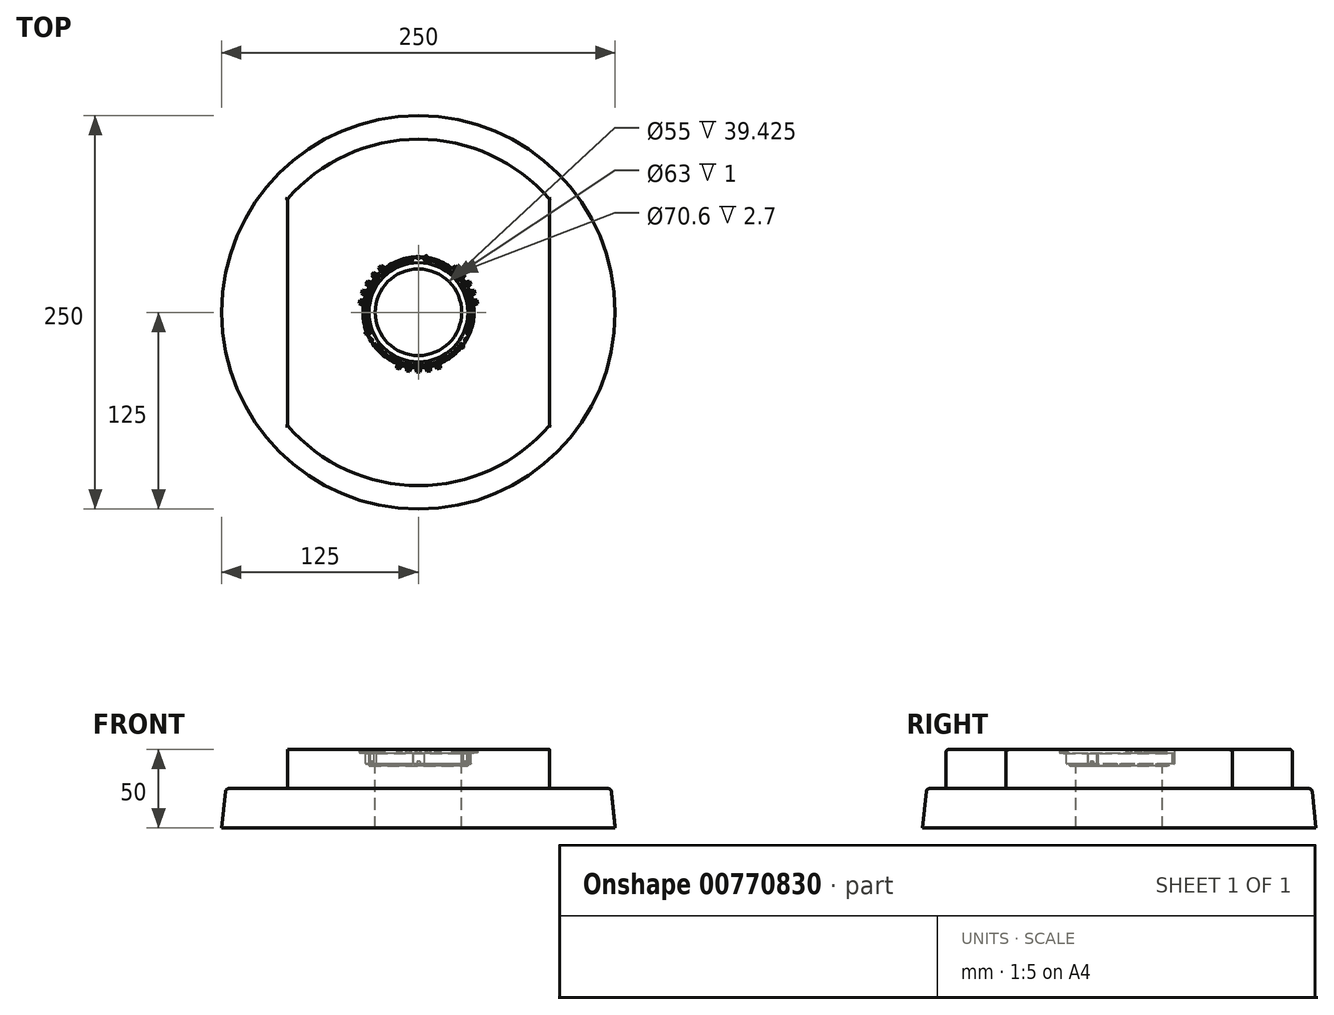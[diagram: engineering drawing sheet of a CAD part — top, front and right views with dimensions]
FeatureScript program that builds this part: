
annotation { "Feature Type Name" : "Feature", "Feature Type Description" : "" }
export const myFeature = defineFeature(function(context is Context, id is Id, definition is map)
    precondition{}
    {
        {
            var Q0;
            Q0=qCreatedBy(makeId("Front.planeOp"),FACE);
            var sketch = newSketch(context, id + "F0", { "sketchPlane" : qUnion([Q0])});
            skLineSegment(sketch, "E0", {"start": v(0, 117.97) * mm, "end": v(0, 0) * mm, "construction": true});
            skLineSegment(sketch, "E1", {"start": v(0, 0) * mm, "end": v(-164.87, 0) * mm, "construction": true});
            skLineSegment(sketch, "E2.bottom", {"start": v(-125, 0) * mm, "end": v(-27.5, 0) * mm});
            skLineSegment(sketch, "E2.top", {"start": v(-110, 50) * mm, "end": v(-37.95, 50) * mm});
            skLineSegment(sketch, "E2.right", {"start": v(0, 0) * mm, "end": v(0, 50) * mm});
            skLineSegment(sketch, "E3", {"start": v(-125, 25) * mm, "end": v(-110, 25) * mm});
            skLineSegment(sketch, "E4", {"start": v(-110, 25) * mm, "end": v(-110, 50) * mm});
            skLineSegment(sketch, "E5", {"start": v(-27.5, 39.43) * mm, "end": v(-27.5, 0) * mm});
            skLineSegment(sketch, "E6", {"start": v(-33.5, 46.85) * mm, "end": v(-33.5, 40.73) * mm});
            skLineSegment(sketch, "E7", {"start": v(-33.5, 40.73) * mm, "end": v(-31.5, 40.73) * mm});
            skLineSegment(sketch, "E8", {"start": v(-31.5, 40.73) * mm, "end": v(-31.5, 39.43) * mm});
            skLineSegment(sketch, "E9", {"start": v(-31.5, 39.43) * mm, "end": v(-27.5, 39.43) * mm});
            skPoint(sketch, "E10.orphan", {"position": v(-27.5, 50) * mm});
            skLineSegment(sketch, "E11", {"start": v(-33.5, 46.85) * mm, "end": v(-33.5, 50) * mm});
            skLineSegment(sketch, "E12", {"start": v(-33.5, 50) * mm, "end": v(-37.95, 50) * mm});
            skLineSegment(sketch, "E13", {"start": v(-125, 0) * mm, "end": v(-125, 25) * mm});
            skLineSegment(sketch, "E14", {"start": v(-125, 0) * mm, "end": v(-122.32, 25) * mm});
            skSolve(sketch);
        }
        {
            var Q0;
            Q0=makeQuery(id+"F0.imprint","IMPRINT",FACE,{"disambiguationData":[TD([[makeQuery(id+"F0.imprint","IMPRINT",EDGE,{"derivedFrom":sQuery(id+"F0.wireOp",EDGE,"E2.bottom")}),1.0]])]});
            var Q1;
            Q1=sQuery(id+"F0.wireOp",EDGE,"E0");
            revolve(context, id + "F1", {"surfaceOperationType" : NewSurfaceOperationType.NEW, "entities" : qUnion([Q0]), "axis" : qUnion([Q1]), "revolveType" : RevolveType.FULL});
        }
        {
            var Q0;
            Q0=makeQuery(id+"F1.opRevolve","SWEPT_FACE",FACE,{"disambiguationData":[OSD([sQuery(id+"F0.wireOp",EDGE,"E2.top"),sQuery(id+"F0.wireOp",EDGE,"E12")])]});
            var sketch = newSketch(context, id + "F2", { "sketchPlane" : qUnion([Q0])});
            skLineSegment(sketch, "E15.bottom", {"start": v(-83.23, 71.92) * mm, "end": v(83.23, 71.92) * mm});
            skLineSegment(sketch, "E15.top", {"start": v(-83.23, -71.92) * mm, "end": v(83.23, -71.92) * mm});
            skLineSegment(sketch, "E15.left", {"start": v(-83.23, 71.92) * mm, "end": v(-83.23, -71.92) * mm});
            skLineSegment(sketch, "E15.right", {"start": v(83.23, 71.92) * mm, "end": v(83.23, -71.92) * mm});
            skPoint(sketch, "E15.middle", {"position": v(0, 0) * mm});
            skCircle(sketch, "E16", {"center": v(0, 0) * mm, "radius": 110 * mm});
            skSolve(sketch);
        }
        {
            var Q0;
            {var subQ0=sQuery(id+"F2.wireOp",EDGE,"E15.right");Q0=makeQuery(id+"F2.imprint","IMPRINT",FACE,{"disambiguationData":[TD([[makeQuery(id+"F2.imprint","IMPRINT",EDGE,{"derivedFrom":subQ0}),1.0]])]});}
            var Q1;
            {var subQ0=sQuery(id+"F2.wireOp",EDGE,"E15.left");Q1=makeQuery(id+"F2.imprint","IMPRINT",FACE,{"disambiguationData":[TD([[makeQuery(id+"F2.imprint","IMPRINT",EDGE,{"derivedFrom":subQ0}),-1.0]])]});}
            extrude(context, id + "F3", {"entities" : qUnion([Q0, Q1]), "operationType" : NewBodyOperationType.REMOVE, "oppositeDirection" : true, "depth" : 25 * mm, "offsetDistance" : 25 * mm});
        }
        {
            var Q0;
            Q0=makeQuery(id+"F3.boolean.opBoolean","SPLIT",EDGE,{"disambiguationData":[OD(1.0)],"derivedFrom":makeQuery(id+"F1.opRevolve","SWEPT_EDGE",EDGE,{"disambiguationData":[OSD([sQuery(id+"F0.wireOp",EDGE,"E2.top"),sQuery(id+"F0.wireOp",EDGE,"E4")])]})});
            var Q1;
            Q1=makeQuery(id+"F3.boolean.opBoolean","COPY",EDGE,{"derivedFrom":makeQuery(id+"F3.opExtrude","CAP_EDGE",EDGE,{"disambiguationData":[OSD([sQuery(id+"F2.wireOp",EDGE,"E15.left")])],"isStart":true})});
            var Q2;
            Q2=makeQuery(id+"F3.boolean.opBoolean","SPLIT",EDGE,{"disambiguationData":[OD(0.0)],"derivedFrom":makeQuery(id+"F1.opRevolve","SWEPT_EDGE",EDGE,{"disambiguationData":[OSD([sQuery(id+"F0.wireOp",EDGE,"E2.top"),sQuery(id+"F0.wireOp",EDGE,"E4")])]})});
            var Q3;
            Q3=makeQuery(id+"F3.boolean.opBoolean","COPY",EDGE,{"derivedFrom":makeQuery(id+"F3.opExtrude","CAP_EDGE",EDGE,{"disambiguationData":[OSD([sQuery(id+"F2.wireOp",EDGE,"E15.right")])],"isStart":true})});
            var Q4;
            Q4=makeQuery(id+"F1.opRevolve","SWEPT_EDGE",EDGE,{"disambiguationData":[OSD([sQuery(id+"F0.wireOp",EDGE,"E3"),sQuery(id+"F0.wireOp",EDGE,"E14")])]});
            fillet(context, id + "F4", {"entities" : qUnion([Q0, Q1, Q2, Q3, Q4]), "radius" : 2 * mm, "tangentPropagation" : true, "allowEdgeOverflow" : false});
        }
        {
            var Q0;
            Q0=makeQuery(id+"F3.boolean.opBoolean","COPY",EDGE,{"derivedFrom":makeQuery(id+"F3.opExtrude","CAP_EDGE",EDGE,{"disambiguationData":[OSD([sQuery(id+"F2.wireOp",EDGE,"E15.left")])],"isStart":false})});
            var Q1;
            Q1=makeQuery(id+"F3.boolean.opBoolean","COPY",EDGE,{"derivedFrom":makeQuery(id+"F3.opExtrude","CAP_EDGE",EDGE,{"disambiguationData":[OSD([sQuery(id+"F2.wireOp",EDGE,"E15.right")])],"isStart":false})});
            var Q2;
            Q2=makeQuery(id+"F3.boolean.opBoolean","SPLIT",EDGE,{"disambiguationData":[OD(0.0)],"derivedFrom":makeQuery(id+"F1.opRevolve","SWEPT_EDGE",EDGE,{"disambiguationData":[OSD([sQuery(id+"F0.wireOp",EDGE,"E3"),sQuery(id+"F0.wireOp",EDGE,"E4")])]})});
            var Q3;
            Q3=makeQuery(id+"F3.boolean.opBoolean","SPLIT",EDGE,{"disambiguationData":[OD(1.0)],"derivedFrom":makeQuery(id+"F1.opRevolve","SWEPT_EDGE",EDGE,{"disambiguationData":[OSD([sQuery(id+"F0.wireOp",EDGE,"E3"),sQuery(id+"F0.wireOp",EDGE,"E4")])]})});
            fillet(context, id + "F5", {"entities" : qUnion([Q0, Q1, Q2, Q3]), "radius" : 1 * mm, "tangentPropagation" : true, "allowEdgeOverflow" : false});
        }
        {
            var Q0;
            Q0=makeQuery(id+"F1.opRevolve","SWEPT_EDGE",EDGE,{"disambiguationData":[OSD([sQuery(id+"F0.wireOp",EDGE,"E8"),sQuery(id+"F0.wireOp",EDGE,"E9")])]});
            fillet(context, id + "F6", {"entities" : qUnion([Q0]), "radius" : .3 * mm, "tangentPropagation" : true, "allowEdgeOverflow" : false});
        }
        {
            var Q0;
            Q0=qCreatedBy(makeId("Front.planeOp"),FACE);
            cPlane(context, id + "F7", {"entities" : qUnion([Q0]), "cplaneType" : CPlaneType.OFFSET, "offset" : 30 * mm, "width" : 150 * mm, "height" : 150 * mm});
        }
        {
            var Q0;
            Q0=qCreatedBy(makeId("Front.planeOp"),FACE);
            cPlane(context, id + "F8", {"entities" : qUnion([Q0]), "cplaneType" : CPlaneType.OFFSET, "offset" : 38 * mm, "width" : 150 * mm, "height" : 150 * mm});
        }
        {
            var Q0;
            Q0=qCreatedBy(id+"F8.planeOp",FACE);
            var sketch = newSketch(context, id + "F9", { "sketchPlane" : qUnion([Q0])});
            skPoint(sketch, "E17.start.orphan", {"position": v(0, 93.3) * mm});
            skLineSegment(sketch, "E18", {"start": v(0, 50) * mm, "end": v(-1.1, 50) * mm});
            skLineSegment(sketch, "E19", {"start": v(0, 100.28) * mm, "end": v(0, 50) * mm, "construction": true});
            skLineSegment(sketch, "E20.MirrorCS", {"start": v(0, 50) * mm, "end": v(1.1, 50) * mm});
            skPoint(sketch, "E21", {"position": v(0, 47.8) * mm});
            skLineSegment(sketch, "E22", {"start": v(-1.1, 50) * mm, "end": v(-1.1, 48.2) * mm});
            skLineSegment(sketch, "E23", {"start": v(-1.1, 48.2) * mm, "end": v(0, 47.8) * mm});
            skLineSegment(sketch, "E24.MirrorCS", {"start": v(1.1, 50) * mm, "end": v(1.1, 48.2) * mm});
            skLineSegment(sketch, "E25.MirrorCS", {"start": v(1.1, 48.2) * mm, "end": v(0, 47.8) * mm});
            skLineSegment(sketch, "E26.trimOffspring", {"start": v(0, 47.8) * mm, "end": v(0, 0) * mm, "construction": true});
            skSolve(sketch);
        }
        {
            var Q0;
            Q0=qCreatedBy(id+"F7.planeOp",FACE);
            var sketch = newSketch(context, id + "F10", { "sketchPlane" : qUnion([Q0])});
            skLineSegment(sketch, "E27", {"start": v(0, 52.95) * mm, "end": v(0, 0) * mm, "construction": true});
            skLineSegment(sketch, "E28", {"start": v(-3, 50) * mm, "end": v(0, 50) * mm});
            skLineSegment(sketch, "E29.MirrorCS", {"start": v(3, 50) * mm, "end": v(0, 50) * mm});
            skLineSegment(sketch, "E30", {"start": v(-3, 50) * mm, "end": v(-3, 48.2) * mm});
            skPoint(sketch, "E31", {"position": v(0, 47.2) * mm});
            skLineSegment(sketch, "E32", {"start": v(-3, 48.2) * mm, "end": v(0, 47.2) * mm});
            skLineSegment(sketch, "E33.MirrorCS", {"start": v(3, 50) * mm, "end": v(3, 48.2) * mm});
            skLineSegment(sketch, "E34.MirrorCS", {"start": v(3, 48.2) * mm, "end": v(0, 47.2) * mm});
            skSolve(sketch);
        }
        {
            var Q0;
            Q0=makeQuery(id+"F9.imprint","IMPRINT",FACE,{"disambiguationData":[TD([[makeQuery(id+"F9.imprint","IMPRINT",EDGE,{"derivedFrom":sQuery(id+"F9.wireOp",EDGE,"E18")}),1.0]])]});
            var Q1;
            Q1=makeQuery(id+"F10.imprint","IMPRINT",FACE,{"disambiguationData":[TD([[makeQuery(id+"F10.imprint","IMPRINT",EDGE,{"derivedFrom":sQuery(id+"F10.wireOp",EDGE,"E28")}),-1.0]])]});
            loft(context, id + "F11", {"operationType" : NewBodyOperationType.REMOVE, "sheetProfilesArray" : [{ "sheetProfileEntities" : qUnion([Q0]) }, { "sheetProfileEntities" : qUnion([Q1]) }]});
        }
        {
            var Q0;
            Q0=makeQuery(id+"F11.boolean.opBoolean","COPY",FACE,{"derivedFrom":makeQuery(id+"F11.opLoft","SWEPT_FACE",FACE,{"disambiguationData":[OSD([sQuery(id+"F9.wireOp",EDGE,"E22"),sQuery(id+"F9.wireOp",EDGE,"E23"),sQuery(id+"F9.wireOp",EDGE,"E25.MirrorCS"),sQuery(id+"F10.wireOp",EDGE,"E30"),sQuery(id+"F10.wireOp",EDGE,"E32"),sQuery(id+"F10.wireOp",EDGE,"E34.MirrorCS")])]})});
            var Q1;
            Q1=makeQuery(id+"F11.boolean.opBoolean","COPY",FACE,{"derivedFrom":makeQuery(id+"F11.opLoft","SWEPT_FACE",FACE,{"disambiguationData":[OSD([sQuery(id+"F9.wireOp",EDGE,"E18"),sQuery(id+"F9.wireOp",EDGE,"E22"),sQuery(id+"F9.wireOp",EDGE,"E23"),sQuery(id+"F10.wireOp",EDGE,"E28"),sQuery(id+"F10.wireOp",EDGE,"E30"),sQuery(id+"F10.wireOp",EDGE,"E32")])]})});
            var Q2;
            Q2=makeQuery(id+"F11.boolean.opBoolean","COPY",FACE,{"derivedFrom":makeQuery(id+"F11.opLoft","SWEPT_FACE",FACE,{"disambiguationData":[OSD([sQuery(id+"F9.wireOp",EDGE,"E23"),sQuery(id+"F9.wireOp",EDGE,"E24.MirrorCS"),sQuery(id+"F9.wireOp",EDGE,"E25.MirrorCS"),sQuery(id+"F10.wireOp",EDGE,"E32"),sQuery(id+"F10.wireOp",EDGE,"E33.MirrorCS"),sQuery(id+"F10.wireOp",EDGE,"E34.MirrorCS")])]})});
            var Q3;
            Q3=makeQuery(id+"F11.boolean.opBoolean","COPY",FACE,{"derivedFrom":makeQuery(id+"F11.opLoft","SWEPT_FACE",FACE,{"disambiguationData":[OSD([sQuery(id+"F9.wireOp",EDGE,"E24.MirrorCS"),sQuery(id+"F9.wireOp",EDGE,"E20.MirrorCS"),sQuery(id+"F9.wireOp",EDGE,"E25.MirrorCS"),sQuery(id+"F10.wireOp",EDGE,"E29.MirrorCS"),sQuery(id+"F10.wireOp",EDGE,"E33.MirrorCS"),sQuery(id+"F10.wireOp",EDGE,"E34.MirrorCS")])]})});
            var Q4;
            Q4=makeQuery(id+"F11.boolean.opBoolean","COPY",FACE,{"derivedFrom":makeQuery(id+"F11.opLoft","CAP_FACE",FACE,{"disambiguationData":[OSD([makeQuery(id+"F9.imprint","IMPRINT",FACE,{"disambiguationData":[TD([[makeQuery(id+"F9.imprint","IMPRINT",EDGE,{"derivedFrom":sQuery(id+"F9.wireOp",EDGE,"E18")}),1.0]])]})])],"isStart":true})});
            var Q5;
            Q5=makeQuery(id+"F1.opRevolve","SWEPT_FACE",FACE,{"disambiguationData":[OSD([sQuery(id+"F0.wireOp",EDGE,"E6"),sQuery(id+"F0.wireOp",EDGE,"E11")])]});
            circularPattern(context, id + "F12", {"patternType" : PatternType.FACE, "faces" : qUnion([Q0, Q1, Q2, Q3, Q4]), "axis" : qUnion([Q5]), "angle" : 20 * degree, "instanceCount" : 3, "equalSpace" : true});
        }
        {
            var Q0;
            Q0=makeQuery(id+"F11.boolean.opBoolean","COPY",FACE,{"derivedFrom":makeQuery(id+"F11.opLoft","SWEPT_FACE",FACE,{"disambiguationData":[OSD([sQuery(id+"F9.wireOp",EDGE,"E22"),sQuery(id+"F9.wireOp",EDGE,"E23"),sQuery(id+"F9.wireOp",EDGE,"E25.MirrorCS"),sQuery(id+"F10.wireOp",EDGE,"E30"),sQuery(id+"F10.wireOp",EDGE,"E32"),sQuery(id+"F10.wireOp",EDGE,"E34.MirrorCS")])]})});
            var Q1;
            Q1=makeQuery(id+"F11.boolean.opBoolean","COPY",FACE,{"derivedFrom":makeQuery(id+"F11.opLoft","SWEPT_FACE",FACE,{"disambiguationData":[OSD([sQuery(id+"F9.wireOp",EDGE,"E18"),sQuery(id+"F9.wireOp",EDGE,"E22"),sQuery(id+"F9.wireOp",EDGE,"E23"),sQuery(id+"F10.wireOp",EDGE,"E28"),sQuery(id+"F10.wireOp",EDGE,"E30"),sQuery(id+"F10.wireOp",EDGE,"E32")])]})});
            var Q2;
            Q2=makeQuery(id+"F11.boolean.opBoolean","COPY",FACE,{"derivedFrom":makeQuery(id+"F11.opLoft","SWEPT_FACE",FACE,{"disambiguationData":[OSD([sQuery(id+"F9.wireOp",EDGE,"E23"),sQuery(id+"F9.wireOp",EDGE,"E24.MirrorCS"),sQuery(id+"F9.wireOp",EDGE,"E25.MirrorCS"),sQuery(id+"F10.wireOp",EDGE,"E32"),sQuery(id+"F10.wireOp",EDGE,"E33.MirrorCS"),sQuery(id+"F10.wireOp",EDGE,"E34.MirrorCS")])]})});
            var Q3;
            Q3=makeQuery(id+"F11.boolean.opBoolean","COPY",FACE,{"derivedFrom":makeQuery(id+"F11.opLoft","SWEPT_FACE",FACE,{"disambiguationData":[OSD([sQuery(id+"F9.wireOp",EDGE,"E24.MirrorCS"),sQuery(id+"F9.wireOp",EDGE,"E20.MirrorCS"),sQuery(id+"F9.wireOp",EDGE,"E25.MirrorCS"),sQuery(id+"F10.wireOp",EDGE,"E29.MirrorCS"),sQuery(id+"F10.wireOp",EDGE,"E33.MirrorCS"),sQuery(id+"F10.wireOp",EDGE,"E34.MirrorCS")])]})});
            var Q4;
            Q4=makeQuery(id+"F11.boolean.opBoolean","COPY",FACE,{"derivedFrom":makeQuery(id+"F11.opLoft","CAP_FACE",FACE,{"disambiguationData":[OSD([makeQuery(id+"F9.imprint","IMPRINT",FACE,{"disambiguationData":[TD([[makeQuery(id+"F9.imprint","IMPRINT",EDGE,{"derivedFrom":sQuery(id+"F9.wireOp",EDGE,"E18")}),1.0]])]})])],"isStart":true})});
            var Q5;
            Q5=makeQuery(id+"F1.opRevolve","SWEPT_FACE",FACE,{"disambiguationData":[OSD([sQuery(id+"F0.wireOp",EDGE,"E6"),sQuery(id+"F0.wireOp",EDGE,"E11")])]});
            circularPattern(context, id + "F13", {"patternType" : PatternType.FACE, "faces" : qUnion([Q0, Q1, Q2, Q3, Q4]), "axis" : qUnion([Q5]), "angle" : 20 * degree, "instanceCount" : 3, "oppositeDirection" : true, "equalSpace" : true});
        }
        {
            var Q0;
            Q0=makeQuery(id+"F12.opPattern","COPY",FACE,{"derivedFrom":makeQuery(id+"F11.boolean.opBoolean","COPY",FACE,{"derivedFrom":makeQuery(id+"F11.opLoft","SWEPT_FACE",FACE,{"disambiguationData":[OSD([sQuery(id+"F9.wireOp",EDGE,"E22"),sQuery(id+"F9.wireOp",EDGE,"E23"),sQuery(id+"F9.wireOp",EDGE,"E25.MirrorCS"),sQuery(id+"F10.wireOp",EDGE,"E30"),sQuery(id+"F10.wireOp",EDGE,"E32"),sQuery(id+"F10.wireOp",EDGE,"E34.MirrorCS")])]})}),"instanceName":"2"});
            var Q1;
            Q1=makeQuery(id+"F12.opPattern","COPY",FACE,{"derivedFrom":makeQuery(id+"F11.boolean.opBoolean","COPY",FACE,{"derivedFrom":makeQuery(id+"F11.opLoft","SWEPT_FACE",FACE,{"disambiguationData":[OSD([sQuery(id+"F9.wireOp",EDGE,"E23"),sQuery(id+"F9.wireOp",EDGE,"E24.MirrorCS"),sQuery(id+"F9.wireOp",EDGE,"E25.MirrorCS"),sQuery(id+"F10.wireOp",EDGE,"E32"),sQuery(id+"F10.wireOp",EDGE,"E33.MirrorCS"),sQuery(id+"F10.wireOp",EDGE,"E34.MirrorCS")])]})}),"instanceName":"2"});
            var Q2;
            Q2=makeQuery(id+"F12.opPattern","COPY",FACE,{"derivedFrom":makeQuery(id+"F11.boolean.opBoolean","COPY",FACE,{"derivedFrom":makeQuery(id+"F11.opLoft","SWEPT_FACE",FACE,{"disambiguationData":[OSD([sQuery(id+"F9.wireOp",EDGE,"E18"),sQuery(id+"F9.wireOp",EDGE,"E22"),sQuery(id+"F9.wireOp",EDGE,"E23"),sQuery(id+"F10.wireOp",EDGE,"E28"),sQuery(id+"F10.wireOp",EDGE,"E30"),sQuery(id+"F10.wireOp",EDGE,"E32")])]})}),"instanceName":"2"});
            var Q3;
            Q3=makeQuery(id+"F12.opPattern","COPY",FACE,{"derivedFrom":makeQuery(id+"F11.boolean.opBoolean","COPY",FACE,{"derivedFrom":makeQuery(id+"F11.opLoft","CAP_FACE",FACE,{"disambiguationData":[OSD([makeQuery(id+"F9.imprint","IMPRINT",FACE,{"disambiguationData":[TD([[makeQuery(id+"F9.imprint","IMPRINT",EDGE,{"derivedFrom":sQuery(id+"F9.wireOp",EDGE,"E18")}),1.0]])]})])],"isStart":true})}),"instanceName":"2"});
            var Q4;
            Q4=makeQuery(id+"F12.opPattern","COPY",FACE,{"derivedFrom":makeQuery(id+"F11.boolean.opBoolean","COPY",FACE,{"derivedFrom":makeQuery(id+"F11.opLoft","SWEPT_FACE",FACE,{"disambiguationData":[OSD([sQuery(id+"F9.wireOp",EDGE,"E24.MirrorCS"),sQuery(id+"F9.wireOp",EDGE,"E20.MirrorCS"),sQuery(id+"F9.wireOp",EDGE,"E25.MirrorCS"),sQuery(id+"F10.wireOp",EDGE,"E29.MirrorCS"),sQuery(id+"F10.wireOp",EDGE,"E33.MirrorCS"),sQuery(id+"F10.wireOp",EDGE,"E34.MirrorCS")])]})}),"instanceName":"2"});
            var Q5;
            Q5=makeQuery(id+"F12.opPattern","COPY",FACE,{"derivedFrom":makeQuery(id+"F11.boolean.opBoolean","COPY",FACE,{"derivedFrom":makeQuery(id+"F11.opLoft","SWEPT_FACE",FACE,{"disambiguationData":[OSD([sQuery(id+"F9.wireOp",EDGE,"E22"),sQuery(id+"F9.wireOp",EDGE,"E23"),sQuery(id+"F9.wireOp",EDGE,"E25.MirrorCS"),sQuery(id+"F10.wireOp",EDGE,"E30"),sQuery(id+"F10.wireOp",EDGE,"E32"),sQuery(id+"F10.wireOp",EDGE,"E34.MirrorCS")])]})}),"instanceName":"1"});
            var Q6;
            Q6=makeQuery(id+"F12.opPattern","COPY",FACE,{"derivedFrom":makeQuery(id+"F11.boolean.opBoolean","COPY",FACE,{"derivedFrom":makeQuery(id+"F11.opLoft","SWEPT_FACE",FACE,{"disambiguationData":[OSD([sQuery(id+"F9.wireOp",EDGE,"E23"),sQuery(id+"F9.wireOp",EDGE,"E24.MirrorCS"),sQuery(id+"F9.wireOp",EDGE,"E25.MirrorCS"),sQuery(id+"F10.wireOp",EDGE,"E32"),sQuery(id+"F10.wireOp",EDGE,"E33.MirrorCS"),sQuery(id+"F10.wireOp",EDGE,"E34.MirrorCS")])]})}),"instanceName":"1"});
            var Q7;
            Q7=makeQuery(id+"F12.opPattern","COPY",FACE,{"derivedFrom":makeQuery(id+"F11.boolean.opBoolean","COPY",FACE,{"derivedFrom":makeQuery(id+"F11.opLoft","SWEPT_FACE",FACE,{"disambiguationData":[OSD([sQuery(id+"F9.wireOp",EDGE,"E18"),sQuery(id+"F9.wireOp",EDGE,"E22"),sQuery(id+"F9.wireOp",EDGE,"E23"),sQuery(id+"F10.wireOp",EDGE,"E28"),sQuery(id+"F10.wireOp",EDGE,"E30"),sQuery(id+"F10.wireOp",EDGE,"E32")])]})}),"instanceName":"1"});
            var Q8;
            Q8=makeQuery(id+"F12.opPattern","COPY",FACE,{"derivedFrom":makeQuery(id+"F11.boolean.opBoolean","COPY",FACE,{"derivedFrom":makeQuery(id+"F11.opLoft","CAP_FACE",FACE,{"disambiguationData":[OSD([makeQuery(id+"F9.imprint","IMPRINT",FACE,{"disambiguationData":[TD([[makeQuery(id+"F9.imprint","IMPRINT",EDGE,{"derivedFrom":sQuery(id+"F9.wireOp",EDGE,"E18")}),1.0]])]})])],"isStart":true})}),"instanceName":"1"});
            var Q9;
            Q9=makeQuery(id+"F12.opPattern","COPY",FACE,{"derivedFrom":makeQuery(id+"F11.boolean.opBoolean","COPY",FACE,{"derivedFrom":makeQuery(id+"F11.opLoft","SWEPT_FACE",FACE,{"disambiguationData":[OSD([sQuery(id+"F9.wireOp",EDGE,"E24.MirrorCS"),sQuery(id+"F9.wireOp",EDGE,"E20.MirrorCS"),sQuery(id+"F9.wireOp",EDGE,"E25.MirrorCS"),sQuery(id+"F10.wireOp",EDGE,"E29.MirrorCS"),sQuery(id+"F10.wireOp",EDGE,"E33.MirrorCS"),sQuery(id+"F10.wireOp",EDGE,"E34.MirrorCS")])]})}),"instanceName":"1"});
            var Q10;
            Q10=makeQuery(id+"F11.boolean.opBoolean","COPY",FACE,{"derivedFrom":makeQuery(id+"F11.opLoft","SWEPT_FACE",FACE,{"disambiguationData":[OSD([sQuery(id+"F9.wireOp",EDGE,"E23"),sQuery(id+"F9.wireOp",EDGE,"E24.MirrorCS"),sQuery(id+"F9.wireOp",EDGE,"E25.MirrorCS"),sQuery(id+"F10.wireOp",EDGE,"E32"),sQuery(id+"F10.wireOp",EDGE,"E33.MirrorCS"),sQuery(id+"F10.wireOp",EDGE,"E34.MirrorCS")])]})});
            var Q11;
            Q11=makeQuery(id+"F11.boolean.opBoolean","COPY",FACE,{"derivedFrom":makeQuery(id+"F11.opLoft","SWEPT_FACE",FACE,{"disambiguationData":[OSD([sQuery(id+"F9.wireOp",EDGE,"E22"),sQuery(id+"F9.wireOp",EDGE,"E23"),sQuery(id+"F9.wireOp",EDGE,"E25.MirrorCS"),sQuery(id+"F10.wireOp",EDGE,"E30"),sQuery(id+"F10.wireOp",EDGE,"E32"),sQuery(id+"F10.wireOp",EDGE,"E34.MirrorCS")])]})});
            var Q12;
            Q12=makeQuery(id+"F11.boolean.opBoolean","COPY",FACE,{"derivedFrom":makeQuery(id+"F11.opLoft","CAP_FACE",FACE,{"disambiguationData":[OSD([makeQuery(id+"F9.imprint","IMPRINT",FACE,{"disambiguationData":[TD([[makeQuery(id+"F9.imprint","IMPRINT",EDGE,{"derivedFrom":sQuery(id+"F9.wireOp",EDGE,"E18")}),1.0]])]})])],"isStart":true})});
            var Q13;
            Q13=makeQuery(id+"F11.boolean.opBoolean","COPY",FACE,{"derivedFrom":makeQuery(id+"F11.opLoft","SWEPT_FACE",FACE,{"disambiguationData":[OSD([sQuery(id+"F9.wireOp",EDGE,"E18"),sQuery(id+"F9.wireOp",EDGE,"E22"),sQuery(id+"F9.wireOp",EDGE,"E23"),sQuery(id+"F10.wireOp",EDGE,"E28"),sQuery(id+"F10.wireOp",EDGE,"E30"),sQuery(id+"F10.wireOp",EDGE,"E32")])]})});
            var Q14;
            Q14=makeQuery(id+"F11.boolean.opBoolean","COPY",FACE,{"derivedFrom":makeQuery(id+"F11.opLoft","SWEPT_FACE",FACE,{"disambiguationData":[OSD([sQuery(id+"F9.wireOp",EDGE,"E24.MirrorCS"),sQuery(id+"F9.wireOp",EDGE,"E20.MirrorCS"),sQuery(id+"F9.wireOp",EDGE,"E25.MirrorCS"),sQuery(id+"F10.wireOp",EDGE,"E29.MirrorCS"),sQuery(id+"F10.wireOp",EDGE,"E33.MirrorCS"),sQuery(id+"F10.wireOp",EDGE,"E34.MirrorCS")])]})});
            var Q15;
            Q15=makeQuery(id+"F13.opPattern","COPY",FACE,{"derivedFrom":makeQuery(id+"F11.boolean.opBoolean","COPY",FACE,{"derivedFrom":makeQuery(id+"F11.opLoft","SWEPT_FACE",FACE,{"disambiguationData":[OSD([sQuery(id+"F9.wireOp",EDGE,"E23"),sQuery(id+"F9.wireOp",EDGE,"E24.MirrorCS"),sQuery(id+"F9.wireOp",EDGE,"E25.MirrorCS"),sQuery(id+"F10.wireOp",EDGE,"E32"),sQuery(id+"F10.wireOp",EDGE,"E33.MirrorCS"),sQuery(id+"F10.wireOp",EDGE,"E34.MirrorCS")])]})}),"instanceName":"1"});
            var Q16;
            Q16=makeQuery(id+"F13.opPattern","COPY",FACE,{"derivedFrom":makeQuery(id+"F11.boolean.opBoolean","COPY",FACE,{"derivedFrom":makeQuery(id+"F11.opLoft","SWEPT_FACE",FACE,{"disambiguationData":[OSD([sQuery(id+"F9.wireOp",EDGE,"E22"),sQuery(id+"F9.wireOp",EDGE,"E23"),sQuery(id+"F9.wireOp",EDGE,"E25.MirrorCS"),sQuery(id+"F10.wireOp",EDGE,"E30"),sQuery(id+"F10.wireOp",EDGE,"E32"),sQuery(id+"F10.wireOp",EDGE,"E34.MirrorCS")])]})}),"instanceName":"1"});
            var Q17;
            Q17=makeQuery(id+"F13.opPattern","COPY",FACE,{"derivedFrom":makeQuery(id+"F11.boolean.opBoolean","COPY",FACE,{"derivedFrom":makeQuery(id+"F11.opLoft","SWEPT_FACE",FACE,{"disambiguationData":[OSD([sQuery(id+"F9.wireOp",EDGE,"E18"),sQuery(id+"F9.wireOp",EDGE,"E22"),sQuery(id+"F9.wireOp",EDGE,"E23"),sQuery(id+"F10.wireOp",EDGE,"E28"),sQuery(id+"F10.wireOp",EDGE,"E30"),sQuery(id+"F10.wireOp",EDGE,"E32")])]})}),"instanceName":"1"});
            var Q18;
            Q18=makeQuery(id+"F13.opPattern","COPY",FACE,{"derivedFrom":makeQuery(id+"F11.boolean.opBoolean","COPY",FACE,{"derivedFrom":makeQuery(id+"F11.opLoft","CAP_FACE",FACE,{"disambiguationData":[OSD([makeQuery(id+"F9.imprint","IMPRINT",FACE,{"disambiguationData":[TD([[makeQuery(id+"F9.imprint","IMPRINT",EDGE,{"derivedFrom":sQuery(id+"F9.wireOp",EDGE,"E18")}),1.0]])]})])],"isStart":true})}),"instanceName":"1"});
            var Q19;
            Q19=makeQuery(id+"F13.opPattern","COPY",FACE,{"derivedFrom":makeQuery(id+"F11.boolean.opBoolean","COPY",FACE,{"derivedFrom":makeQuery(id+"F11.opLoft","SWEPT_FACE",FACE,{"disambiguationData":[OSD([sQuery(id+"F9.wireOp",EDGE,"E24.MirrorCS"),sQuery(id+"F9.wireOp",EDGE,"E20.MirrorCS"),sQuery(id+"F9.wireOp",EDGE,"E25.MirrorCS"),sQuery(id+"F10.wireOp",EDGE,"E29.MirrorCS"),sQuery(id+"F10.wireOp",EDGE,"E33.MirrorCS"),sQuery(id+"F10.wireOp",EDGE,"E34.MirrorCS")])]})}),"instanceName":"1"});
            var Q20;
            Q20=makeQuery(id+"F13.opPattern","COPY",FACE,{"derivedFrom":makeQuery(id+"F11.boolean.opBoolean","COPY",FACE,{"derivedFrom":makeQuery(id+"F11.opLoft","SWEPT_FACE",FACE,{"disambiguationData":[OSD([sQuery(id+"F9.wireOp",EDGE,"E22"),sQuery(id+"F9.wireOp",EDGE,"E23"),sQuery(id+"F9.wireOp",EDGE,"E25.MirrorCS"),sQuery(id+"F10.wireOp",EDGE,"E30"),sQuery(id+"F10.wireOp",EDGE,"E32"),sQuery(id+"F10.wireOp",EDGE,"E34.MirrorCS")])]})}),"instanceName":"2"});
            var Q21;
            Q21=makeQuery(id+"F13.opPattern","COPY",FACE,{"derivedFrom":makeQuery(id+"F11.boolean.opBoolean","COPY",FACE,{"derivedFrom":makeQuery(id+"F11.opLoft","SWEPT_FACE",FACE,{"disambiguationData":[OSD([sQuery(id+"F9.wireOp",EDGE,"E23"),sQuery(id+"F9.wireOp",EDGE,"E24.MirrorCS"),sQuery(id+"F9.wireOp",EDGE,"E25.MirrorCS"),sQuery(id+"F10.wireOp",EDGE,"E32"),sQuery(id+"F10.wireOp",EDGE,"E33.MirrorCS"),sQuery(id+"F10.wireOp",EDGE,"E34.MirrorCS")])]})}),"instanceName":"2"});
            var Q22;
            Q22=makeQuery(id+"F13.opPattern","COPY",FACE,{"derivedFrom":makeQuery(id+"F11.boolean.opBoolean","COPY",FACE,{"derivedFrom":makeQuery(id+"F11.opLoft","SWEPT_FACE",FACE,{"disambiguationData":[OSD([sQuery(id+"F9.wireOp",EDGE,"E18"),sQuery(id+"F9.wireOp",EDGE,"E22"),sQuery(id+"F9.wireOp",EDGE,"E23"),sQuery(id+"F10.wireOp",EDGE,"E28"),sQuery(id+"F10.wireOp",EDGE,"E30"),sQuery(id+"F10.wireOp",EDGE,"E32")])]})}),"instanceName":"2"});
            var Q23;
            Q23=makeQuery(id+"F13.opPattern","COPY",FACE,{"derivedFrom":makeQuery(id+"F11.boolean.opBoolean","COPY",FACE,{"derivedFrom":makeQuery(id+"F11.opLoft","CAP_FACE",FACE,{"disambiguationData":[OSD([makeQuery(id+"F9.imprint","IMPRINT",FACE,{"disambiguationData":[TD([[makeQuery(id+"F9.imprint","IMPRINT",EDGE,{"derivedFrom":sQuery(id+"F9.wireOp",EDGE,"E18")}),1.0]])]})])],"isStart":true})}),"instanceName":"2"});
            var Q24;
            Q24=makeQuery(id+"F13.opPattern","COPY",FACE,{"derivedFrom":makeQuery(id+"F11.boolean.opBoolean","COPY",FACE,{"derivedFrom":makeQuery(id+"F11.opLoft","SWEPT_FACE",FACE,{"disambiguationData":[OSD([sQuery(id+"F9.wireOp",EDGE,"E24.MirrorCS"),sQuery(id+"F9.wireOp",EDGE,"E20.MirrorCS"),sQuery(id+"F9.wireOp",EDGE,"E25.MirrorCS"),sQuery(id+"F10.wireOp",EDGE,"E29.MirrorCS"),sQuery(id+"F10.wireOp",EDGE,"E33.MirrorCS"),sQuery(id+"F10.wireOp",EDGE,"E34.MirrorCS")])]})}),"instanceName":"2"});
            var Q25;
            Q25=makeQuery(id+"F1.opRevolve","SWEPT_FACE",FACE,{"disambiguationData":[OSD([sQuery(id+"F0.wireOp",EDGE,"E6"),sQuery(id+"F0.wireOp",EDGE,"E11")])]});
            circularPattern(context, id + "F14", {"patternType" : PatternType.FACE, "faces" : qUnion([Q0, Q1, Q2, Q3, Q4, Q5, Q6, Q7, Q8, Q9, Q10, Q11, Q12, Q13, Q14, Q15, Q16, Q17, Q18, Q19, Q20, Q21, Q22, Q23, Q24]), "axis" : qUnion([Q25]), "angle" : 360 * degree, "instanceCount" : 3, "equalSpace" : true});
        }
        {
            var Q0;
            Q0=makeQuery(id+"F1.opRevolve","SWEPT_FACE",FACE,{"disambiguationData":[OSD([sQuery(id+"F0.wireOp",EDGE,"E2.top"),sQuery(id+"F0.wireOp",EDGE,"E12")])]});
            var sketch = newSketch(context, id + "F15", { "sketchPlane" : qUnion([Q0])});
            skCircle(sketch, "E35", {"center": v(0, 0) * mm, "radius": 33.5 * mm});
            skCircle(sketch, "E36", {"center": v(0, 0) * mm, "radius": 35.3 * mm});
            skLineSegment(sketch, "E37", {"start": v(0, 52.04) * mm, "end": v(0, 0) * mm, "construction": true});
            skLineSegment(sketch, "E38", {"start": v(-3.4, 35.14) * mm, "end": v(-3.63, 33.3) * mm});
            skLineSegment(sketch, "E39.MirrorCS", {"start": v(3.4, 35.14) * mm, "end": v(3.63, 33.3) * mm});
            skLineSegment(sketch, "E40.1.0", {"start": v(-28.73, -20.51) * mm, "end": v(-27.03, -19.8) * mm});
            skLineSegment(sketch, "E40.1.1", {"start": v(-32.13, -14.62) * mm, "end": v(-30.66, -13.5) * mm});
            skLineSegment(sketch, "E40.2.0", {"start": v(32.13, -14.62) * mm, "end": v(30.66, -13.5) * mm});
            skLineSegment(sketch, "E40.2.1", {"start": v(28.73, -20.51) * mm, "end": v(27.03, -19.8) * mm});
            skSolve(sketch);
        }
        {
            var Q0;
            Q0 = qSketchRegion(id + "F15", true);
            extrude(context, id + "F16", {"entities" : qUnion([Q0]), "operationType" : NewBodyOperationType.REMOVE, "oppositeDirection" : true, "depth" : 2.7 * mm, "offsetDistance" : 25 * mm});
        }
        {
            var Q0;
            Q0=makeQuery(id+"F1.opRevolve","SWEPT_FACE",FACE,{"disambiguationData":[OSD([sQuery(id+"F0.wireOp",EDGE,"E7")])]});
            var sketch = newSketch(context, id + "F17", { "sketchPlane" : qUnion([Q0])});
            skCircle(sketch, "E41", {"center": v(0, 0) * mm, "radius": 34.9 * mm});
            skCircle(sketch, "E42", {"center": v(0, 0) * mm, "radius": 33.5 * mm});
            skLineSegment(sketch, "E43", {"start": v(0, 42) * mm, "end": v(0, 0) * mm, "construction": true});
            skLineSegment(sketch, "E44", {"start": v(-3.4, 35.14) * mm, "end": v(-3.63, 33.3) * mm});
            skLineSegment(sketch, "E45.MirrorCS", {"start": v(3.4, 35.14) * mm, "end": v(3.63, 33.3) * mm});
            skLineSegment(sketch, "E46.1.0", {"start": v(-28.73, -20.51) * mm, "end": v(-27.03, -19.8) * mm});
            skLineSegment(sketch, "E46.1.1", {"start": v(-32.13, -14.62) * mm, "end": v(-30.66, -13.5) * mm});
            skLineSegment(sketch, "E46.2.0", {"start": v(32.13, -14.62) * mm, "end": v(30.66, -13.5) * mm});
            skLineSegment(sketch, "E46.2.1", {"start": v(28.73, -20.51) * mm, "end": v(27.03, -19.8) * mm});
            skSolve(sketch);
        }
        {
            var Q0;
            {var subQ0=sQuery(id+"F15.wireOp",EDGE,"E38");Q0=makeQuery(id+"F15.imprint","IMPRINT",FACE,{"disambiguationData":[TD([[makeQuery(id+"F15.imprint","IMPRINT",EDGE,{"derivedFrom":subQ0}),1.0]])]});}
            var Q1;
            {var subQ0=sQuery(id+"F15.wireOp",EDGE,"E40.1.0");Q1=makeQuery(id+"F15.imprint","IMPRINT",FACE,{"disambiguationData":[TD([[makeQuery(id+"F15.imprint","IMPRINT",EDGE,{"derivedFrom":subQ0}),1.0]])]});}
            var Q2;
            {var subQ0=sQuery(id+"F15.wireOp",EDGE,"E40.2.0");Q2=makeQuery(id+"F15.imprint","IMPRINT",FACE,{"disambiguationData":[TD([[makeQuery(id+"F15.imprint","IMPRINT",EDGE,{"derivedFrom":subQ0}),1.0]])]});}
            extrude(context, id + "F18", {"entities" : qUnion([Q0, Q1, Q2]), "operationType" : NewBodyOperationType.REMOVE, "depth" : 25 * mm, "offsetDistance" : 25 * mm});
        }
        {
            var Q0;
            {var subQ0=sQuery(id+"F17.wireOp",EDGE,"E44");var subQ1=sQuery(id+"F17.wireOp",EDGE,"E41");var subQ2=makeQuery(id+"F17.imprint","INTERSECT",VERTEX,{"derivedFrom":[subQ1,subQ0]});Q0=makeQuery(id+"F17.imprint","IMPRINT",FACE,{"disambiguationData":[TD([[makeQuery(id+"F17.imprint","IMPRINT",EDGE,{"disambiguationData":[TD([[subQ2,1.0]])],"derivedFrom":subQ1}),1.0]])]});}
            var Q1;
            {var subQ0=sQuery(id+"F17.wireOp",EDGE,"E46.1.1");var subQ1=sQuery(id+"F17.wireOp",EDGE,"E41");var subQ2=makeQuery(id+"F17.imprint","INTERSECT",VERTEX,{"derivedFrom":[subQ1,subQ0]});Q1=makeQuery(id+"F17.imprint","IMPRINT",FACE,{"disambiguationData":[TD([[makeQuery(id+"F17.imprint","IMPRINT",EDGE,{"disambiguationData":[TD([[subQ2,-1.0]])],"derivedFrom":subQ1}),1.0]])]});}
            var Q2;
            {var subQ0=sQuery(id+"F17.wireOp",EDGE,"E46.2.1");var subQ1=sQuery(id+"F17.wireOp",EDGE,"E41");var subQ2=makeQuery(id+"F17.imprint","INTERSECT",VERTEX,{"derivedFrom":[subQ1,subQ0]});Q2=makeQuery(id+"F17.imprint","IMPRINT",FACE,{"disambiguationData":[TD([[makeQuery(id+"F17.imprint","IMPRINT",EDGE,{"disambiguationData":[TD([[subQ2,-1.0]])],"derivedFrom":subQ1}),1.0]])]});}
            extrude(context, id + "F19", {"entities" : qUnion([Q0, Q1, Q2]), "operationType" : NewBodyOperationType.REMOVE, "depth" : 25 * mm, "offsetDistance" : 25 * mm});
        }
        {
            var Q0;
            {var subQ3=sQuery(id+"F17.wireOp",EDGE,"E44");var subQ4=sQuery(id+"F0.wireOp",EDGE,"E7");var subQ5=sQuery(id+"F0.wireOp",EDGE,"E6");Q0=makeQuery(id+"F19.boolean.opBoolean","SPLIT",EDGE,{"disambiguationData":[TD([makeQuery(id+"F19.opExtrude","SWEPT_FACE",FACE,{"disambiguationData":[OSD([subQ3])]})])],"derivedFrom":makeQuery(id+"F1.opRevolve","SWEPT_EDGE",EDGE,{"disambiguationData":[OSD([subQ5,subQ4])]})});}
            var Q1;
            {var subQ2=sQuery(id+"F17.wireOp",EDGE,"E45.MirrorCS");var subQ3=sQuery(id+"F0.wireOp",EDGE,"E7");var subQ5=sQuery(id+"F0.wireOp",EDGE,"E6");Q1=makeQuery(id+"F19.boolean.opBoolean","SPLIT",EDGE,{"disambiguationData":[TD([makeQuery(id+"F19.opExtrude","SWEPT_FACE",FACE,{"disambiguationData":[OSD([subQ2])]})])],"derivedFrom":makeQuery(id+"F1.opRevolve","SWEPT_EDGE",EDGE,{"disambiguationData":[OSD([subQ5,subQ3])]})});}
            var Q2;
            {var subQ0=sQuery(id+"F17.wireOp",EDGE,"E46.1.0");var subQ3=sQuery(id+"F0.wireOp",EDGE,"E7");var subQ5=sQuery(id+"F0.wireOp",EDGE,"E6");Q2=makeQuery(id+"F19.boolean.opBoolean","SPLIT",EDGE,{"disambiguationData":[TD([makeQuery(id+"F19.opExtrude","SWEPT_FACE",FACE,{"disambiguationData":[OSD([subQ0])]})])],"derivedFrom":makeQuery(id+"F1.opRevolve","SWEPT_EDGE",EDGE,{"disambiguationData":[OSD([subQ5,subQ3])]})});}
            var Q3;
            {var subQ0=sQuery(id+"F15.wireOp",EDGE,"E35");Q3=makeQuery(id+"F19.boolean.opBoolean","SPLIT",EDGE,{"disambiguationData":[TD([makeQuery(id+"F19.opExtrude","SWEPT_FACE",FACE,{"disambiguationData":[OSD([sQuery(id+"F17.wireOp",EDGE,"E46.1.0")])]})])],"derivedFrom":makeQuery(id+"F16.boolean.opBoolean","COPY",EDGE,{"derivedFrom":makeQuery(id+"F16.opExtrude","CAP_EDGE",EDGE,{"disambiguationData":[OSD([subQ0])],"isStart":false})})});}
            var Q4;
            {var subQ0=sQuery(id+"F15.wireOp",EDGE,"E35");Q4=makeQuery(id+"F19.boolean.opBoolean","SPLIT",EDGE,{"disambiguationData":[TD([makeQuery(id+"F19.opExtrude","SWEPT_FACE",FACE,{"disambiguationData":[OSD([sQuery(id+"F17.wireOp",EDGE,"E45.MirrorCS")])]})])],"derivedFrom":makeQuery(id+"F16.boolean.opBoolean","COPY",EDGE,{"derivedFrom":makeQuery(id+"F16.opExtrude","CAP_EDGE",EDGE,{"disambiguationData":[OSD([subQ0])],"isStart":false})})});}
            var Q5;
            {var subQ0=sQuery(id+"F15.wireOp",EDGE,"E35");Q5=makeQuery(id+"F19.boolean.opBoolean","SPLIT",EDGE,{"disambiguationData":[TD([makeQuery(id+"F19.opExtrude","SWEPT_FACE",FACE,{"disambiguationData":[OSD([sQuery(id+"F17.wireOp",EDGE,"E44")])]})])],"derivedFrom":makeQuery(id+"F16.boolean.opBoolean","COPY",EDGE,{"derivedFrom":makeQuery(id+"F16.opExtrude","CAP_EDGE",EDGE,{"disambiguationData":[OSD([subQ0])],"isStart":false})})});}
            fillet(context, id + "F20", {"entities" : qUnion([Q0, Q1, Q2, Q3, Q4, Q5]), "radius" : .2 * mm, "tangentPropagation" : true, "allowEdgeOverflow" : false});
        }
        {
            var Q0;
            {var subQ0=sQuery(id+"F17.wireOp",EDGE,"E42");var subQ1=sQuery(id+"F17.wireOp",EDGE,"E41");Q0=makeQuery(id+"F19.boolean.opBoolean","MERGE",FACE,{"derivedFrom":[makeQuery(id+"F1.opRevolve","SWEPT_FACE",FACE,{"disambiguationData":[OSD([sQuery(id+"F0.wireOp",EDGE,"E7")])]}),makeQuery(id+"F19.opExtrude","CAP_FACE",FACE,{"disambiguationData":[OSD([subQ1,subQ0,sQuery(id+"F17.wireOp",EDGE,"E44"),sQuery(id+"F17.wireOp",EDGE,"E45.MirrorCS")])],"isStart":true}),makeQuery(id+"F19.opExtrude","CAP_FACE",FACE,{"disambiguationData":[OSD([subQ1,subQ0,sQuery(id+"F17.wireOp",EDGE,"E46.1.0"),sQuery(id+"F17.wireOp",EDGE,"E46.1.1")])],"isStart":true}),makeQuery(id+"F19.opExtrude","CAP_FACE",FACE,{"disambiguationData":[OSD([subQ1,subQ0,sQuery(id+"F17.wireOp",EDGE,"E46.2.0"),sQuery(id+"F17.wireOp",EDGE,"E46.2.1")])],"isStart":true})]});}
            var sketch = newSketch(context, id + "F21", { "sketchPlane" : qUnion([Q0])});
            skLineSegment(sketch, "E47", {"start": v(0, 127.93) * mm, "end": v(0, 0) * mm, "construction": true});
            skLineSegment(sketch, "E48", {"start": v(0, 0) * mm, "end": v(-170.85, 0) * mm, "construction": true});
            skCircle(sketch, "E49", {"center": v(0, 0) * mm, "radius": 34.9 * mm});
            skArc(sketch, "E50", {"start": v(-1, 34.89) * mm, "mid": v(0, 33.9) * mm, "end": v(1, 34.89) * mm});
            skArc(sketch, "E51.1.0", {"start": v(-29.7, -18.31) * mm, "mid": v(-29.35, -16.95) * mm, "end": v(-30.71, -16.57) * mm});
            skArc(sketch, "E51.2.0", {"start": v(30.71, -16.57) * mm, "mid": v(29.35, -16.95) * mm, "end": v(29.7, -18.31) * mm});
            skSolve(sketch);
        }
        {
            var Q0;
            {var subQ0=sQuery(id+"F21.wireOp",EDGE,"E51.1.0");Q0=makeQuery(id+"F21.imprint","IMPRINT",FACE,{"disambiguationData":[TD([[makeQuery(id+"F21.imprint","IMPRINT",EDGE,{"derivedFrom":subQ0}),1.0]])]});}
            var Q1;
            {var subQ0=sQuery(id+"F21.wireOp",EDGE,"E51.2.0");Q1=makeQuery(id+"F21.imprint","IMPRINT",FACE,{"disambiguationData":[TD([[makeQuery(id+"F21.imprint","IMPRINT",EDGE,{"derivedFrom":subQ0}),1.0]])]});}
            var Q2;
            {var subQ0=sQuery(id+"F21.wireOp",EDGE,"E50");Q2=makeQuery(id+"F21.imprint","IMPRINT",FACE,{"disambiguationData":[TD([[makeQuery(id+"F21.imprint","IMPRINT",EDGE,{"derivedFrom":subQ0}),1.0]])]});}
            extrude(context, id + "F22", {"entities" : qUnion([Q0, Q1, Q2]), "depth" : 1.5 * mm, "offsetDistance" : 25 * mm});
        }
        {
            var Q0;
            Q0=makeQuery(id+"F1.opRevolve","SWEPT_FACE",FACE,{"disambiguationData":[OSD([sQuery(id+"F0.wireOp",EDGE,"E2.top"),sQuery(id+"F0.wireOp",EDGE,"E12")])]});
            var sketch = newSketch(context, id + "F23", { "sketchPlane" : qUnion([Q0])});
            skCircle(sketch, "E52", {"center": v(0, 0) * mm, "radius": 35.3 * mm});
            skArc(sketch, "E53", {"start": v(4.14, 35.46) * mm, "mid": v(-28.08, 22.05) * mm, "end": v(-33.47, -12.43) * mm});
            skLineSegment(sketch, "E54", {"start": v(0, 77.91) * mm, "end": v(0, 0) * mm, "construction": true});
            skArc(sketch, "E55", {"start": v(5.99, 34.79) * mm, "mid": v(5.14, 35.93) * mm, "end": v(4, 35.07) * mm});
            skArc(sketch, "E56.1.0", {"start": v(-33.12, -12.2) * mm, "mid": v(-33.7, -13.51) * mm, "end": v(-32.38, -14.06) * mm});
            skArc(sketch, "E56.2.0", {"start": v(27.13, -22.58) * mm, "mid": v(28.55, -22.42) * mm, "end": v(28.37, -21) * mm});
            skArc(sketch, "E57.trimOffspring", {"start": v(28.64, -21.32) * mm, "mid": v(33.13, 13.3) * mm, "end": v(5.97, 35.2) * mm});
            skArc(sketch, "E58.trimOffspring", {"start": v(-32.78, -14.14) * mm, "mid": v(-5.06, -35.34) * mm, "end": v(27.5, -22.77) * mm});
            skSolve(sketch);
        }
        {
            var Q0;
            {var subQ0=sQuery(id+"F23.wireOp",EDGE,"E55");var subQ1=sQuery(id+"F23.wireOp",EDGE,"E52");var subQ2=makeQuery(id+"F23.imprint","INTERSECT",VERTEX,{"disambiguationData":[OD(0.0)],"derivedFrom":[subQ1,subQ0]});Q0=makeQuery(id+"F23.imprint","IMPRINT",FACE,{"disambiguationData":[TD([[makeQuery(id+"F23.imprint","IMPRINT",EDGE,{"disambiguationData":[TD([[subQ2,-1.0]])],"derivedFrom":subQ1}),-1.0]])]});}
            var Q1;
            {var subQ0=sQuery(id+"F23.wireOp",EDGE,"E56.2.0");var subQ1=sQuery(id+"F23.wireOp",EDGE,"E52");var subQ2=makeQuery(id+"F23.imprint","INTERSECT",VERTEX,{"disambiguationData":[OD(0.0)],"derivedFrom":[subQ1,subQ0]});Q1=makeQuery(id+"F23.imprint","IMPRINT",FACE,{"disambiguationData":[TD([[makeQuery(id+"F23.imprint","IMPRINT",EDGE,{"disambiguationData":[TD([[subQ2,-1.0]])],"derivedFrom":subQ1}),-1.0]])]});}
            var Q2;
            {var subQ0=sQuery(id+"F23.wireOp",EDGE,"E56.1.0");var subQ1=sQuery(id+"F23.wireOp",EDGE,"E52");var subQ2=makeQuery(id+"F23.imprint","INTERSECT",VERTEX,{"disambiguationData":[OD(0.0)],"derivedFrom":[subQ1,subQ0]});Q2=makeQuery(id+"F23.imprint","IMPRINT",FACE,{"disambiguationData":[TD([[makeQuery(id+"F23.imprint","IMPRINT",EDGE,{"disambiguationData":[TD([[subQ2,-1.0]])],"derivedFrom":subQ1}),-1.0]])]});}
            extrude(context, id + "F24", {"entities" : qUnion([Q0, Q1, Q2]), "operationType" : NewBodyOperationType.REMOVE, "oppositeDirection" : true, "depth" : .5 * mm, "offsetDistance" : 25 * mm});
        }
    });
